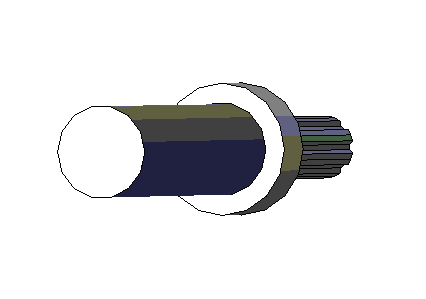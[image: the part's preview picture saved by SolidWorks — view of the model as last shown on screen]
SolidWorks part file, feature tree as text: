
SOLIDWORKS PART (.sldprt)
format: sldprt  version: not decoded by parser v0  size: 176,128 bytes
history: native  units: mm
features: sketch x5, extrude x5, chamfer x1 (+10 scaffold rows collapsed)
feature tree (21):
  scaffold x10  (default folders/planes/origin — collapsed)
  sketch  "Sketch1"  dims[D1=1.905mm]
  extrude  "Extrude1"  Depth=7.874mm
  sketch  "Sketch5"  dims[D1=~5.531505deg]
  extrude  "Extrude3"  Depth=7.874mm
  chamfer  "Chamfer4"  Distance=0.127mm Angle=45deg
  sketch  "Sketch6"
  extrude  "Extrude4"  Depth=0.635mm
  sketch  "Sketch7"  dims[D1=4.699mm]
  extrude  "Extrude5"  Depth=1.905mm
  sketch  "Sketch8"  dims[D1=3.302mm]
  extrude  "Extrude6"  Depth=12.319mm
decode coverage: 10 of 11 modeling features carry decoded parameters
note: ~ marks probable driven/reference dimensions
note: suppression state not decoded; provenance and decode notes live in map.json
